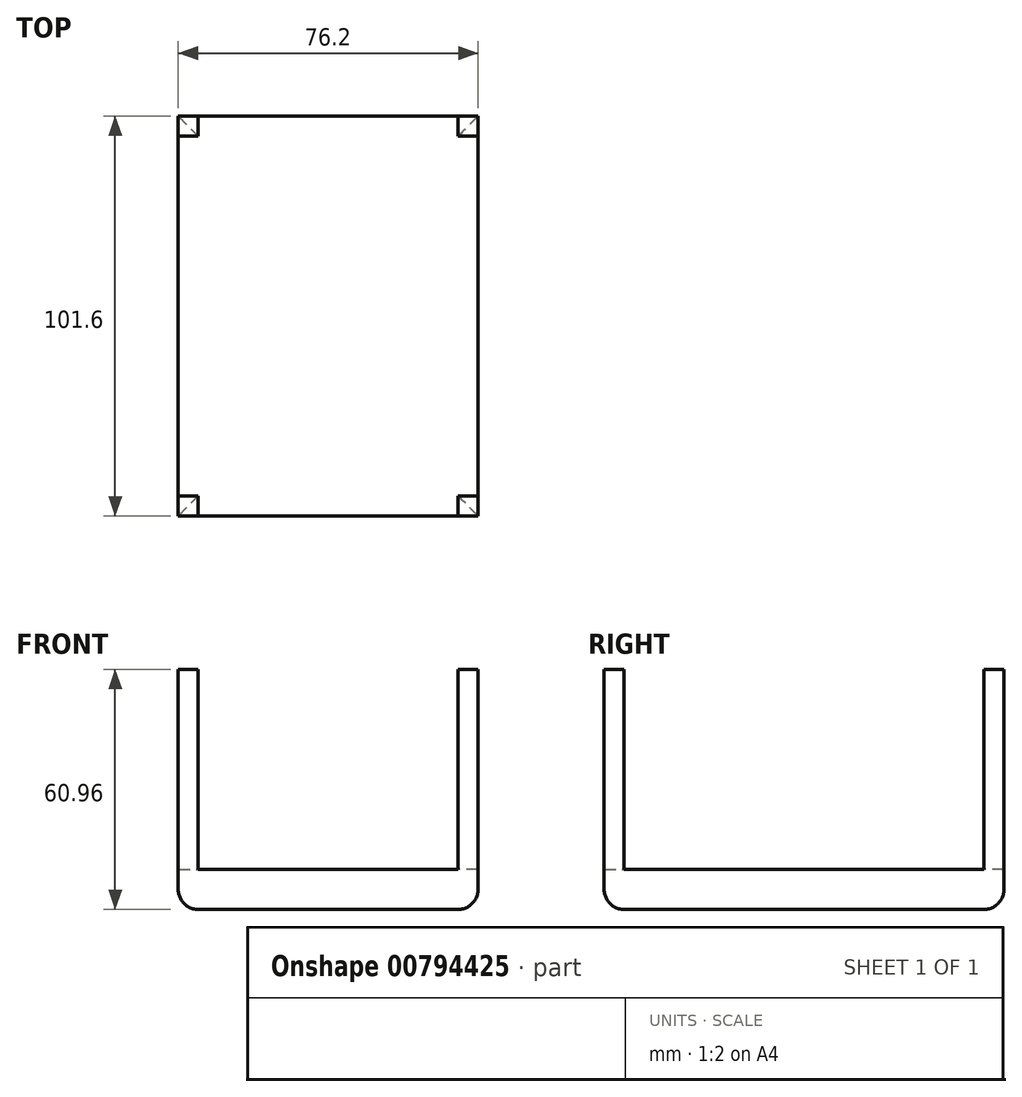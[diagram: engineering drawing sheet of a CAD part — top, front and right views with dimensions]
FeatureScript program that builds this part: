
annotation { "Feature Type Name" : "Feature", "Feature Type Description" : "" }
export const myFeature = defineFeature(function(context is Context, id is Id, definition is map)
    precondition{}
    {
        {
            var Q0;
            Q0=qCreatedBy(makeId("Top.planeOp"),FACE);
            var sketch = newSketch(context, id + "F0", { "sketchPlane" : qUnion([Q0])});
            skPoint(sketch, "E0.middle", {"position": v(0, 0) * mm});
            skLineSegment(sketch, "E1.bottom", {"start": v(38.1, -50.8) * mm, "end": v(-38.1, -50.8) * mm});
            skLineSegment(sketch, "E1.top", {"start": v(38.1, 50.8) * mm, "end": v(-38.1, 50.8) * mm});
            skLineSegment(sketch, "E1.left", {"start": v(38.1, -50.8) * mm, "end": v(38.1, 50.8) * mm});
            skLineSegment(sketch, "E1.right", {"start": v(-38.1, -50.8) * mm, "end": v(-38.1, 50.8) * mm});
            skSolve(sketch);
        }
        {
            var Q0;
            Q0=makeQuery(id+"F0.imprint","IMPRINT",FACE,{"disambiguationData":[TD([[makeQuery(id+"F0.imprint","IMPRINT",EDGE,{"derivedFrom":sQuery(id+"F0.wireOp",EDGE,"E1.bottom")}),-1.0]])]});
            extrude(context, id + "F1", {"entities" : qUnion([Q0]), "depth" : 10.16 * mm, "offsetDistance" : 25.4 * mm});
        }
        {
            var Q0;
            Q0=makeQuery(id+"F1.opExtrude","CAP_FACE",FACE,{"disambiguationData":[OSD([sQuery(id+"F0.wireOp",EDGE,"E1.bottom"),sQuery(id+"F0.wireOp",EDGE,"E1.top"),sQuery(id+"F0.wireOp",EDGE,"E1.left"),sQuery(id+"F0.wireOp",EDGE,"E1.right")])],"isStart":false});
            var sketch = newSketch(context, id + "F2", { "sketchPlane" : qUnion([Q0])});
            skLineSegment(sketch, "E2.bottom", {"start": v(-38.1, 50.8) * mm, "end": v(-33.02, 50.8) * mm});
            skLineSegment(sketch, "E2.top", {"start": v(-38.1, 45.72) * mm, "end": v(-33.02, 45.72) * mm});
            skLineSegment(sketch, "E2.left", {"start": v(-38.1, 50.8) * mm, "end": v(-38.1, 45.72) * mm});
            skLineSegment(sketch, "E2.right", {"start": v(-33.02, 50.8) * mm, "end": v(-33.02, 45.72) * mm});
            skLineSegment(sketch, "E3.bottom", {"start": v(38.1, 50.8) * mm, "end": v(33.02, 50.8) * mm});
            skLineSegment(sketch, "E3.top", {"start": v(38.1, 45.72) * mm, "end": v(33.02, 45.72) * mm});
            skLineSegment(sketch, "E3.left", {"start": v(38.1, 50.8) * mm, "end": v(38.1, 45.72) * mm});
            skLineSegment(sketch, "E3.right", {"start": v(33.02, 50.8) * mm, "end": v(33.02, 45.72) * mm});
            skLineSegment(sketch, "E4.bottom", {"start": v(38.1, -50.8) * mm, "end": v(33.02, -50.8) * mm});
            skLineSegment(sketch, "E4.top", {"start": v(38.1, -45.72) * mm, "end": v(33.02, -45.72) * mm});
            skLineSegment(sketch, "E4.left", {"start": v(38.1, -50.8) * mm, "end": v(38.1, -45.72) * mm});
            skLineSegment(sketch, "E4.right", {"start": v(33.02, -50.8) * mm, "end": v(33.02, -45.72) * mm});
            skLineSegment(sketch, "E5.bottom", {"start": v(-38.1, -50.8) * mm, "end": v(-33.02, -50.8) * mm});
            skLineSegment(sketch, "E5.top", {"start": v(-38.1, -45.72) * mm, "end": v(-33.02, -45.72) * mm});
            skLineSegment(sketch, "E5.left", {"start": v(-38.1, -50.8) * mm, "end": v(-38.1, -45.72) * mm});
            skLineSegment(sketch, "E5.right", {"start": v(-33.02, -50.8) * mm, "end": v(-33.02, -45.72) * mm});
            skSolve(sketch);
        }
        {
            var Q0;
            Q0=makeQuery(id+"F2.imprint","IMPRINT",FACE,{"disambiguationData":[TD([[makeQuery(id+"F2.imprint","IMPRINT",EDGE,{"derivedFrom":sQuery(id+"F2.wireOp",EDGE,"E3.bottom")}),1.0]])]});
            var Q1;
            Q1=makeQuery(id+"F2.imprint","IMPRINT",FACE,{"disambiguationData":[TD([[makeQuery(id+"F2.imprint","IMPRINT",EDGE,{"derivedFrom":sQuery(id+"F2.wireOp",EDGE,"E4.bottom")}),-1.0]])]});
            var Q2;
            Q2=makeQuery(id+"F2.imprint","IMPRINT",FACE,{"disambiguationData":[TD([[makeQuery(id+"F2.imprint","IMPRINT",EDGE,{"derivedFrom":sQuery(id+"F2.wireOp",EDGE,"E2.bottom")}),1.0]])]});
            var Q3;
            Q3=makeQuery(id+"F2.imprint","IMPRINT",FACE,{"disambiguationData":[TD([[makeQuery(id+"F2.imprint","IMPRINT",EDGE,{"derivedFrom":sQuery(id+"F2.wireOp",EDGE,"E5.bottom")}),-1.0]])]});
            extrude(context, id + "F3", {"entities" : qUnion([Q0, Q1, Q2, Q3]), "operationType" : NewBodyOperationType.ADD, "depth" : 50.8 * mm, "offsetDistance" : 25.4 * mm});
        }
        {
            var Q0;
            Q0=makeQuery(id+"F1.opExtrude","CAP_EDGE",EDGE,{"disambiguationData":[OSD([sQuery(id+"F0.wireOp",EDGE,"E1.top")])],"isStart":true});
            var Q1;
            Q1=makeQuery(id+"F1.opExtrude","CAP_EDGE",EDGE,{"disambiguationData":[OSD([sQuery(id+"F0.wireOp",EDGE,"E1.left")])],"isStart":true});
            var Q2;
            Q2=makeQuery(id+"F1.opExtrude","CAP_EDGE",EDGE,{"disambiguationData":[OSD([sQuery(id+"F0.wireOp",EDGE,"E1.bottom")])],"isStart":true});
            var Q3;
            Q3=makeQuery(id+"F1.opExtrude","CAP_EDGE",EDGE,{"disambiguationData":[OSD([sQuery(id+"F0.wireOp",EDGE,"E1.right")])],"isStart":true});
            fillet(context, id + "F4", {"entities" : qUnion([Q0, Q1, Q2, Q3]), "radius" : 5.08 * mm, "tangentPropagation" : true, "allowEdgeOverflow" : false});
        }
    });
